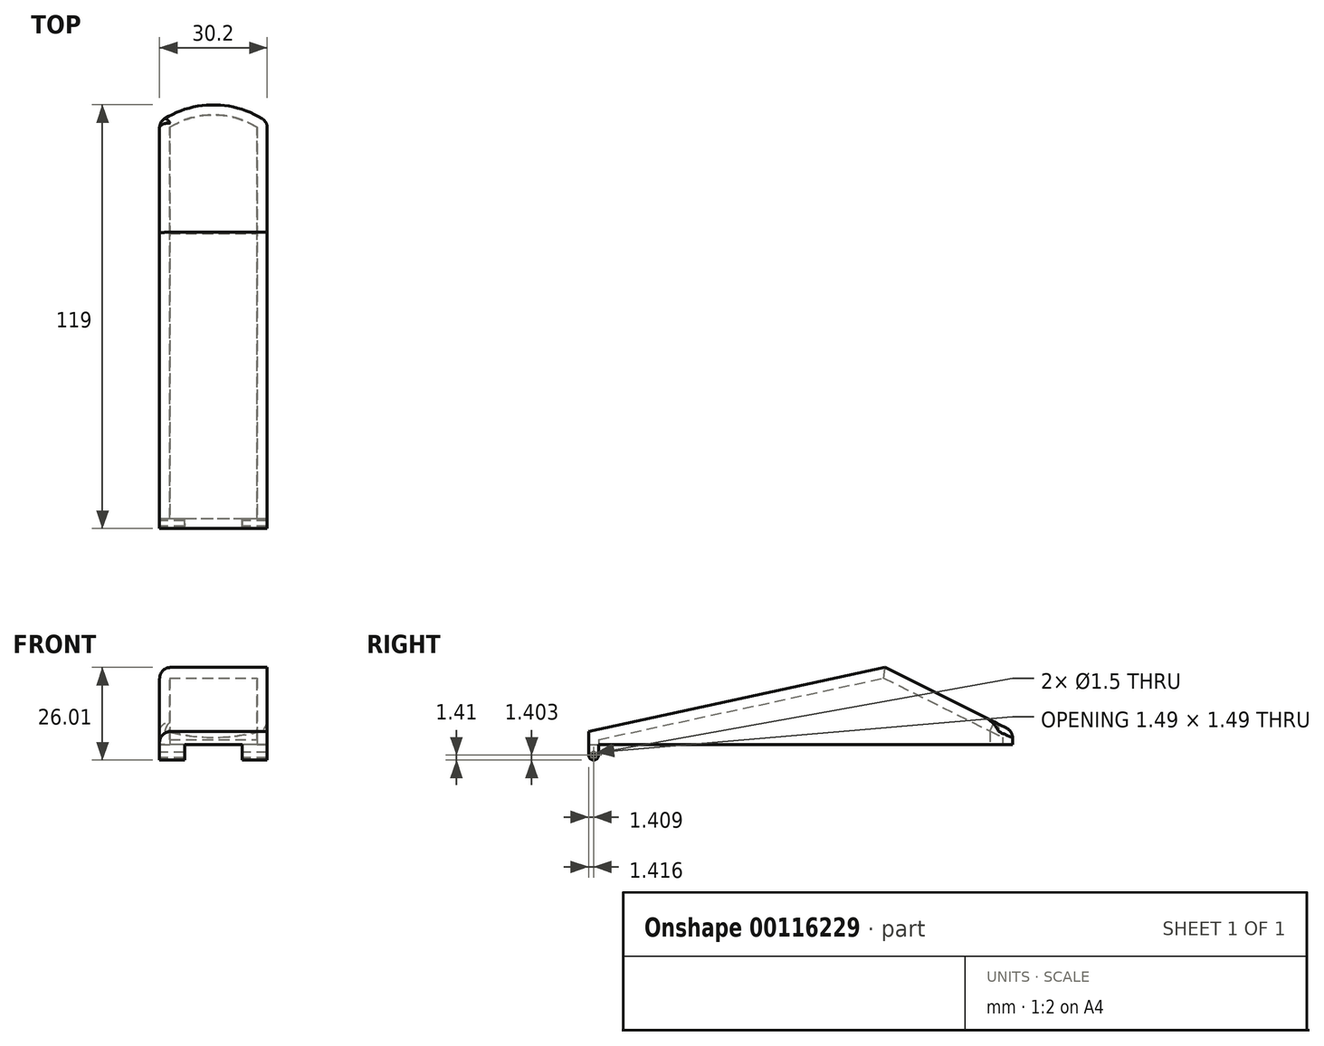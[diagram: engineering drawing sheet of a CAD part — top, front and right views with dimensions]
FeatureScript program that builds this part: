
annotation { "Feature Type Name" : "Feature", "Feature Type Description" : "" }
export const myFeature = defineFeature(function(context is Context, id is Id, definition is map)
    precondition{}
    {
        {
            var Q0;
            Q0=qCreatedBy(makeId("Right.planeOp"),FACE);
            cPlane(context, id + "F0", {"entities" : qUnion([Q0]), "cplaneType" : CPlaneType.OFFSET, "offset" : 6.07 * mm, "oppositeDirection" : true, "width" : 150 * mm, "height" : 150 * mm});
        }
        {
            var Q0;
            Q0=qCreatedBy(makeId("Top.planeOp"),FACE);
            var sketch = newSketch(context, id + "F1", { "sketchPlane" : qUnion([Q0])});
            skLineSegment(sketch, "E0.top", {"start": v(-21.07, -85.23) * mm, "end": v(9.13, -85.23) * mm});
            skLineSegment(sketch, "E0.left", {"start": v(-21.07, 28.93) * mm, "end": v(-21.07, -85.23) * mm});
            skLineSegment(sketch, "E0.right", {"start": v(9.13, 28.93) * mm, "end": v(9.13, -85.23) * mm});
            skArc(sketch, "E1", {"start": v(9.13, 28.93) * mm, "mid": v(-5.97, 33.77) * mm, "end": v(-21.07, 28.93) * mm});
            skLineSegment(sketch, "E2", {"start": v(-89.3, 33.77) * mm, "end": v(90.29, 33.77) * mm});
            skLineSegment(sketch, "E3.bottom", {"start": v(-21.07, 4.77) * mm, "end": v(-21.47, 4.77) * mm});
            skLineSegment(sketch, "E3.top", {"start": v(-21.07, 3.07) * mm, "end": v(-21.47, 3.07) * mm});
            skLineSegment(sketch, "E3.left", {"start": v(-21.07, 4.77) * mm, "end": v(-21.07, 3.07) * mm});
            skLineSegment(sketch, "E3.right", {"start": v(-21.47, 4.77) * mm, "end": v(-21.47, 3.07) * mm});
            skLineSegment(sketch, "E4.1.0.0", {"start": v(-21.47, 1.47) * mm, "end": v(-21.47, -0.23) * mm});
            skLineSegment(sketch, "E4.1.0.1", {"start": v(-21.07, 1.47) * mm, "end": v(-21.47, 1.47) * mm});
            skLineSegment(sketch, "E4.1.0.2", {"start": v(-21.07, -0.23) * mm, "end": v(-21.47, -0.23) * mm});
            skLineSegment(sketch, "E4.2.0.0", {"start": v(-21.47, -1.83) * mm, "end": v(-21.47, -3.53) * mm});
            skLineSegment(sketch, "E4.2.0.1", {"start": v(-21.07, -1.83) * mm, "end": v(-21.47, -1.83) * mm});
            skLineSegment(sketch, "E4.2.0.2", {"start": v(-21.07, -3.53) * mm, "end": v(-21.47, -3.53) * mm});
            skLineSegment(sketch, "E4.3.0.0", {"start": v(-21.47, -5.13) * mm, "end": v(-21.47, -6.83) * mm});
            skLineSegment(sketch, "E4.3.0.1", {"start": v(-21.07, -5.13) * mm, "end": v(-21.47, -5.13) * mm});
            skLineSegment(sketch, "E4.3.0.2", {"start": v(-21.07, -6.83) * mm, "end": v(-21.47, -6.83) * mm});
            skLineSegment(sketch, "E4.4.0.0", {"start": v(-21.47, -8.43) * mm, "end": v(-21.47, -10.13) * mm});
            skLineSegment(sketch, "E4.4.0.1", {"start": v(-21.07, -8.43) * mm, "end": v(-21.47, -8.43) * mm});
            skLineSegment(sketch, "E4.4.0.2", {"start": v(-21.07, -10.13) * mm, "end": v(-21.47, -10.13) * mm});
            skLineSegment(sketch, "E4.direction1", {"start": v(-21.47, 3.07) * mm, "end": v(-21.47, -0.23) * mm, "construction": true});
            skLineSegment(sketch, "E5.MirrorCS", {"start": v(-21.87, 4.77) * mm, "end": v(-21.47, 4.77) * mm});
            skLineSegment(sketch, "E6.MirrorCS", {"start": v(-21.87, 3.07) * mm, "end": v(-21.47, 3.07) * mm});
            skLineSegment(sketch, "E7.MirrorCS", {"start": v(8.93, 4.77) * mm, "end": v(9.33, 4.77) * mm});
            skLineSegment(sketch, "E8.MirrorCS", {"start": v(9.33, 4.77) * mm, "end": v(9.33, 3.07) * mm});
            skLineSegment(sketch, "E9.MirrorCS", {"start": v(8.93, 3.07) * mm, "end": v(9.33, 3.07) * mm});
            skLineSegment(sketch, "E10.MirrorCS", {"start": v(8.93, 1.47) * mm, "end": v(9.33, 1.47) * mm});
            skLineSegment(sketch, "E11.MirrorCS", {"start": v(9.33, 3.07) * mm, "end": v(9.33, -0.23) * mm, "construction": true});
            skLineSegment(sketch, "E12.MirrorCS", {"start": v(8.93, -0.23) * mm, "end": v(9.33, -0.23) * mm});
            skLineSegment(sketch, "E13.MirrorCS", {"start": v(8.93, -1.83) * mm, "end": v(9.33, -1.83) * mm});
            skLineSegment(sketch, "E14.MirrorCS", {"start": v(9.33, -1.83) * mm, "end": v(9.33, -3.53) * mm});
            skLineSegment(sketch, "E15.MirrorCS", {"start": v(8.93, -3.53) * mm, "end": v(9.33, -3.53) * mm});
            skLineSegment(sketch, "E16.MirrorCS", {"start": v(8.93, -5.13) * mm, "end": v(9.33, -5.13) * mm});
            skLineSegment(sketch, "E17.MirrorCS", {"start": v(9.33, -5.13) * mm, "end": v(9.33, -6.83) * mm});
            skLineSegment(sketch, "E18.MirrorCS", {"start": v(8.93, -6.83) * mm, "end": v(9.33, -6.83) * mm});
            skLineSegment(sketch, "E19.MirrorCS", {"start": v(8.93, -8.43) * mm, "end": v(9.33, -8.43) * mm});
            skLineSegment(sketch, "E20.MirrorCS", {"start": v(9.33, -8.43) * mm, "end": v(9.33, -10.13) * mm});
            skLineSegment(sketch, "E21.MirrorCS", {"start": v(8.93, -10.13) * mm, "end": v(9.33, -10.13) * mm});
            skSolve(sketch);
        }
        {
            var Q0;
            Q0=makeQuery(id+"F1.imprint","IMPRINT",FACE,{"disambiguationData":[TD([[makeQuery(id+"F1.imprint","IMPRINT",EDGE,{"derivedFrom":sQuery(id+"F1.wireOp",EDGE,"E0.top")}),1.0]])]});
            extrude(context, id + "F2", {"entities" : qUnion([Q0]), "depth" : 21.6 * mm});
        }
        {
            var Q0;
            Q0=makeQuery(id+"F2.opExtrude","SWEPT_FACE",FACE,{"disambiguationData":[OSD([sQuery(id+"F1.wireOp",EDGE,"E0.right")])]});
            var sketch = newSketch(context, id + "F3", { "sketchPlane" : qUnion([Q0])});
            skLineSegment(sketch, "E22", {"start": v(34, 3.6) * mm, "end": v(34, 0) * mm});
            skLineSegment(sketch, "E23", {"start": v(-85.23, 3.6) * mm, "end": v(-85.23, 0) * mm});
            skLineSegment(sketch, "E24", {"start": v(-85.23, 0) * mm, "end": v(34, 0) * mm});
            skLineSegment(sketch, "E25", {"start": v(-2, 21.6) * mm, "end": v(-2, 0) * mm});
            skLineSegment(sketch, "E26", {"start": v(-85.23, 3.6) * mm, "end": v(-2, 21.6) * mm});
            skLineSegment(sketch, "E27", {"start": v(-2, 21.6) * mm, "end": v(34, 3.6) * mm});
            skLineSegment(sketch, "E28", {"start": v(-85.23, 3.6) * mm, "end": v(-85.23, 44.89) * mm});
            skLineSegment(sketch, "E29", {"start": v(-85.23, 44.89) * mm, "end": v(34, 44.89) * mm});
            skLineSegment(sketch, "E30", {"start": v(34, 3.6) * mm, "end": v(34, 44.89) * mm});
            skSolve(sketch);
        }
        {
            var Q0;
            {var subQ1=sQuery(id+"F3.wireOp",EDGE,"E29");Q0=makeQuery(id+"F3.imprint","IMPRINT",FACE,{"disambiguationData":[TD([[makeQuery(id+"F3.imprint","IMPRINT",EDGE,{"derivedFrom":subQ1}),-1.0]])]});}
            var Q1;
            {var subQ0=sQuery(id+"F3.wireOp",EDGE,"E26");Q1=makeQuery(id+"F3.imprint","IMPRINT",FACE,{"disambiguationData":[TD([[makeQuery(id+"F3.imprint","IMPRINT",EDGE,{"derivedFrom":subQ0}),1.0]])]});}
            var Q2;
            {var subQ0=sQuery(id+"F3.wireOp",EDGE,"E27");var subQ1=sQuery(id+"F1.wireOp",EDGE,"E0.right");var subQ4=makeQuery(id+"F2.opExtrude","SWEPT_EDGE",EDGE,{"disambiguationData":[OSD([subQ1,sQuery(id+"F1.wireOp",EDGE,"E1")])]});var subQ5=makeQuery(id+"F3.imprint","INTERSECT",VERTEX,{"derivedFrom":[subQ4,subQ0]});Q2=makeQuery(id+"F3.imprint","IMPRINT",FACE,{"disambiguationData":[TD([[makeQuery(id+"F3.imprint","IMPRINT",EDGE,{"disambiguationData":[TD([[subQ5,1.0]])],"derivedFrom":subQ0}),1.0]])]});}
            extrude(context, id + "F4", {"entities" : qUnion([Q0, Q1, Q2]), "operationType" : NewBodyOperationType.REMOVE, "oppositeDirection" : true, "depth" : 40 * mm});
        }
        {
            var Q0;
            Q0=makeQuery(id+"F2.opExtrude","CAP_FACE",FACE,{"disambiguationData":[OSD([sQuery(id+"F1.wireOp",EDGE,"E0.top"),sQuery(id+"F1.wireOp",EDGE,"E0.left"),sQuery(id+"F1.wireOp",EDGE,"E0.right"),sQuery(id+"F1.wireOp",EDGE,"E1")])],"isStart":true});
            shell(context, id + "F5", {"entities" : qUnion([Q0]), "thickness" : 2.82 * mm});
        }
        {
            var Q0;
            Q0=makeQuery(id+"F4.boolean.opBoolean","INTERSECT",EDGE,{"derivedFrom":[makeQuery(id+"F2.opExtrude","SWEPT_FACE",FACE,{"disambiguationData":[OSD([sQuery(id+"F1.wireOp",EDGE,"E0.left")])]}),makeQuery(id+"F4.opExtrude","SWEPT_FACE",FACE,{"disambiguationData":[OSD([sQuery(id+"F3.wireOp",EDGE,"E27")])]})]});
            var Q1;
            Q1=makeQuery(id+"F4.boolean.opBoolean","COPY",EDGE,{"derivedFrom":makeQuery(id+"F4.opExtrude","CAP_EDGE",EDGE,{"disambiguationData":[OSD([sQuery(id+"F3.wireOp",EDGE,"E27")])],"isStart":true})});
            var Q2;
            Q2=makeQuery(id+"F4.boolean.opBoolean","COPY",EDGE,{"derivedFrom":makeQuery(id+"F4.opExtrude","CAP_EDGE",EDGE,{"disambiguationData":[OSD([sQuery(id+"F3.wireOp",EDGE,"E26")])],"isStart":true})});
            var Q3;
            Q3=makeQuery(id+"F4.boolean.opBoolean","INTERSECT",EDGE,{"derivedFrom":[makeQuery(id+"F2.opExtrude","SWEPT_FACE",FACE,{"disambiguationData":[OSD([sQuery(id+"F1.wireOp",EDGE,"E0.left")])]}),makeQuery(id+"F4.opExtrude","SWEPT_FACE",FACE,{"disambiguationData":[OSD([sQuery(id+"F3.wireOp",EDGE,"E26")])]})]});
            var Q4;
            Q4=makeQuery(id+"F4.boolean.opBoolean","COPY",EDGE,{"derivedFrom":makeQuery(id+"F4.opExtrude","SWEPT_EDGE",EDGE,{"disambiguationData":[OSD([sQuery(id+"F3.wireOp",EDGE,"E23"),sQuery(id+"F3.wireOp",EDGE,"E26"),sQuery(id+"F3.wireOp",EDGE,"E28")])]})});
            var Q5;
            Q5=makeQuery(id+"F4.boolean.opBoolean","INTERSECT",EDGE,{"derivedFrom":[makeQuery(id+"F2.opExtrude","SWEPT_FACE",FACE,{"disambiguationData":[OSD([sQuery(id+"F1.wireOp",EDGE,"E1")])]}),makeQuery(id+"F4.opExtrude","SWEPT_FACE",FACE,{"disambiguationData":[OSD([sQuery(id+"F3.wireOp",EDGE,"E27")])]})]});
            var Q6;
            Q6=makeQuery(id+"F2.opExtrude","SWEPT_EDGE",EDGE,{"disambiguationData":[OSD([sQuery(id+"F1.wireOp",EDGE,"E0.right"),sQuery(id+"F1.wireOp",EDGE,"E1")])]});
            var Q7;
            Q7=makeQuery(id+"F2.opExtrude","SWEPT_EDGE",EDGE,{"disambiguationData":[OSD([sQuery(id+"F1.wireOp",EDGE,"E0.left"),sQuery(id+"F1.wireOp",EDGE,"E1")])]});
            fillet(context, id + "F6", {"entities" : qUnion([Q0, Q1, Q2, Q3, Q4, Q5, Q6, Q7]), "radius" : 3 * mm, "tangentPropagation" : true, "allowEdgeOverflow" : false});
        }
        {
            var Q0;
            {var subQ10=sQuery(id+"F1.wireOp",EDGE,"E0.top");Q0=makeQuery(id+"F1.imprint","IMPRINT",FACE,{"disambiguationData":[TD([[makeQuery(id+"F1.imprint","IMPRINT",EDGE,{"derivedFrom":subQ10}),1.0]])]});}
            var sketch = newSketch(context, id + "F7", { "sketchPlane" : qUnion([Q0])});
            skLineSegment(sketch, "E31.bottom", {"start": v(-21.07, -85.23) * mm, "end": v(-14.07, -85.23) * mm});
            skLineSegment(sketch, "E31.top", {"start": v(-21.07, -82.41) * mm, "end": v(-14.07, -82.41) * mm});
            skLineSegment(sketch, "E31.left", {"start": v(-21.07, -85.23) * mm, "end": v(-21.07, -82.41) * mm});
            skLineSegment(sketch, "E31.right", {"start": v(-14.07, -85.23) * mm, "end": v(-14.07, -82.41) * mm});
            skLineSegment(sketch, "E32.bottom", {"start": v(2.13, -85.23) * mm, "end": v(9.13, -85.23) * mm});
            skLineSegment(sketch, "E32.top", {"start": v(2.13, -82.41) * mm, "end": v(9.13, -82.41) * mm});
            skLineSegment(sketch, "E32.left", {"start": v(2.13, -85.23) * mm, "end": v(2.13, -82.41) * mm});
            skLineSegment(sketch, "E32.right", {"start": v(9.13, -85.23) * mm, "end": v(9.13, -82.41) * mm});
            skSolve(sketch);
        }
        {
            var Q0;
            Q0 = qSketchRegion(id + "F7", true);
            extrude(context, id + "F8", {"entities" : qUnion([Q0]), "operationType" : NewBodyOperationType.ADD, "oppositeDirection" : true, "depth" : 3 * mm});
        }
        {
            var Q0;
            Q0=makeQuery(id+"F8.boolean.opBoolean","MERGE",FACE,{"derivedFrom":[makeQuery(id+"F2.opExtrude","SWEPT_FACE",FACE,{"disambiguationData":[OSD([sQuery(id+"F1.wireOp",EDGE,"E0.left"),sQuery(id+"F1.wireOp",EDGE,"E3.left")])]}),makeQuery(id+"F8.opExtrude","SWEPT_FACE",FACE,{"disambiguationData":[OSD([sQuery(id+"F7.wireOp",EDGE,"E31.left")])]})]});
            var sketch = newSketch(context, id + "F9", { "sketchPlane" : qUnion([Q0])});
            skArc(sketch, "E33", {"start": v(82.41, -3) * mm, "mid": v(83.82, -4.4) * mm, "end": v(85.23, -3) * mm});
            skSolve(sketch);
        }
        {
            var Q0;
            Q0=makeQuery(id+"F9.imprint","IMPRINT",FACE,{"disambiguationData":[TD([[makeQuery(id+"F9.imprint","IMPRINT",EDGE,{"derivedFrom":sQuery(id+"F9.wireOp",EDGE,"E33")}),1.0]])]});
            var Q1;
            Q1=makeQuery(id+"F8.opExtrude","SWEPT_FACE",FACE,{"disambiguationData":[OSD([sQuery(id+"F7.wireOp",EDGE,"E31.right")])]});
            extrude(context, id + "F10", {"entities" : qUnion([Q0]), "operationType" : NewBodyOperationType.ADD, "endBound" : BoundingType.UP_TO_SURFACE, "oppositeDirection" : true, "endBoundEntityFace" : qUnion([Q1]), "depth" : 25 * mm});
        }
        {
            var Q0;
            Q0=makeQuery(id+"F8.opExtrude","SWEPT_FACE",FACE,{"disambiguationData":[OSD([sQuery(id+"F7.wireOp",EDGE,"E32.left")])]});
            var sketch = newSketch(context, id + "F11", { "sketchPlane" : qUnion([Q0])});
            skArc(sketch, "E34", {"start": v(82.41, -3) * mm, "mid": v(83.82, -4.41) * mm, "end": v(85.23, -3) * mm});
            skSolve(sketch);
        }
        {
            var Q0;
            Q0 = qSketchRegion(id + "F11", true);
            var Q1;
            Q1=makeQuery(id+"F11.imprint","IMPRINT",FACE,{"disambiguationData":[TD([[makeQuery(id+"F11.imprint","IMPRINT",EDGE,{"derivedFrom":sQuery(id+"F11.wireOp",EDGE,"E34")}),1.0]])]});
            var Q2;
            Q2=makeQuery(id+"F8.boolean.opBoolean","MERGE",FACE,{"derivedFrom":[makeQuery(id+"F2.opExtrude","SWEPT_FACE",FACE,{"disambiguationData":[OSD([sQuery(id+"F1.wireOp",EDGE,"E0.right")])]}),makeQuery(id+"F8.opExtrude","SWEPT_FACE",FACE,{"disambiguationData":[OSD([sQuery(id+"F7.wireOp",EDGE,"E32.right")])]})]});
            extrude(context, id + "F12", {"entities" : qUnion([Q0, Q1]), "operationType" : NewBodyOperationType.ADD, "endBound" : BoundingType.UP_TO_SURFACE, "oppositeDirection" : true, "endBoundEntityFace" : qUnion([Q2]), "depth" : 25 * mm});
        }
        {
            var Q0;
            {var subQ0=sQuery(id+"F7.wireOp",EDGE,"E31.left");Q0=makeQuery(id+"F10.boolean.opBoolean","MERGE",FACE,{"derivedFrom":[makeQuery(id+"F8.boolean.opBoolean","MERGE",FACE,{"derivedFrom":[makeQuery(id+"F2.opExtrude","SWEPT_FACE",FACE,{"disambiguationData":[OSD([sQuery(id+"F1.wireOp",EDGE,"E0.left"),sQuery(id+"F1.wireOp",EDGE,"E3.left")])]}),makeQuery(id+"F8.opExtrude","SWEPT_FACE",FACE,{"disambiguationData":[OSD([subQ0])]})]}),makeQuery(id+"F10.opExtrude","CAP_FACE",FACE,{"disambiguationData":[OSD([subQ0,sQuery(id+"F9.wireOp",EDGE,"E33")])],"isStart":true})]});}
            var sketch = newSketch(context, id + "F13", { "sketchPlane" : qUnion([Q0])});
            skCircle(sketch, "E35", {"center": v(83.82, -3) * mm, "radius": 0.75 * mm});
            skSolve(sketch);
        }
        {
            var Q0;
            Q0 = qSketchRegion(id + "F13", true);
            var Q1;
            {var subQ0=sQuery(id+"F7.wireOp",EDGE,"E32.right");var subQ1=sQuery(id+"F1.wireOp",EDGE,"E0.right");Q1=makeQuery(id+"F12.boolean.opBoolean","MERGE",FACE,{"derivedFrom":[makeQuery(id+"F8.boolean.opBoolean","MERGE",FACE,{"derivedFrom":[makeQuery(id+"F2.opExtrude","SWEPT_FACE",FACE,{"disambiguationData":[OSD([subQ1])]}),makeQuery(id+"F8.opExtrude","SWEPT_FACE",FACE,{"disambiguationData":[OSD([subQ0])]})]}),makeQuery(id+"F12.opExtrude","CAP_FACE",FACE,{"disambiguationData":[OSD([subQ1,subQ0])],"isStart":false})]});}
            var Q2;
            {var subQ0=sQuery(id+"F7.wireOp",EDGE,"E32.right");var subQ1=sQuery(id+"F1.wireOp",EDGE,"E0.right");Q2=makeQuery(id+"F12.boolean.opBoolean","MERGE",FACE,{"derivedFrom":[makeQuery(id+"F8.boolean.opBoolean","MERGE",FACE,{"derivedFrom":[makeQuery(id+"F2.opExtrude","SWEPT_FACE",FACE,{"disambiguationData":[OSD([subQ1])]}),makeQuery(id+"F8.opExtrude","SWEPT_FACE",FACE,{"disambiguationData":[OSD([subQ0])]})]}),makeQuery(id+"F12.opExtrude","CAP_FACE",FACE,{"disambiguationData":[OSD([subQ1,subQ0])],"isStart":false})]});}
            extrude(context, id + "F14", {"entities" : qUnion([Q0, Q1]), "operationType" : NewBodyOperationType.REMOVE, "endBound" : BoundingType.THROUGH_ALL, "oppositeDirection" : true, "endBoundEntityFace" : qUnion([Q2]), "depth" : 25 * mm});
        }
    });
